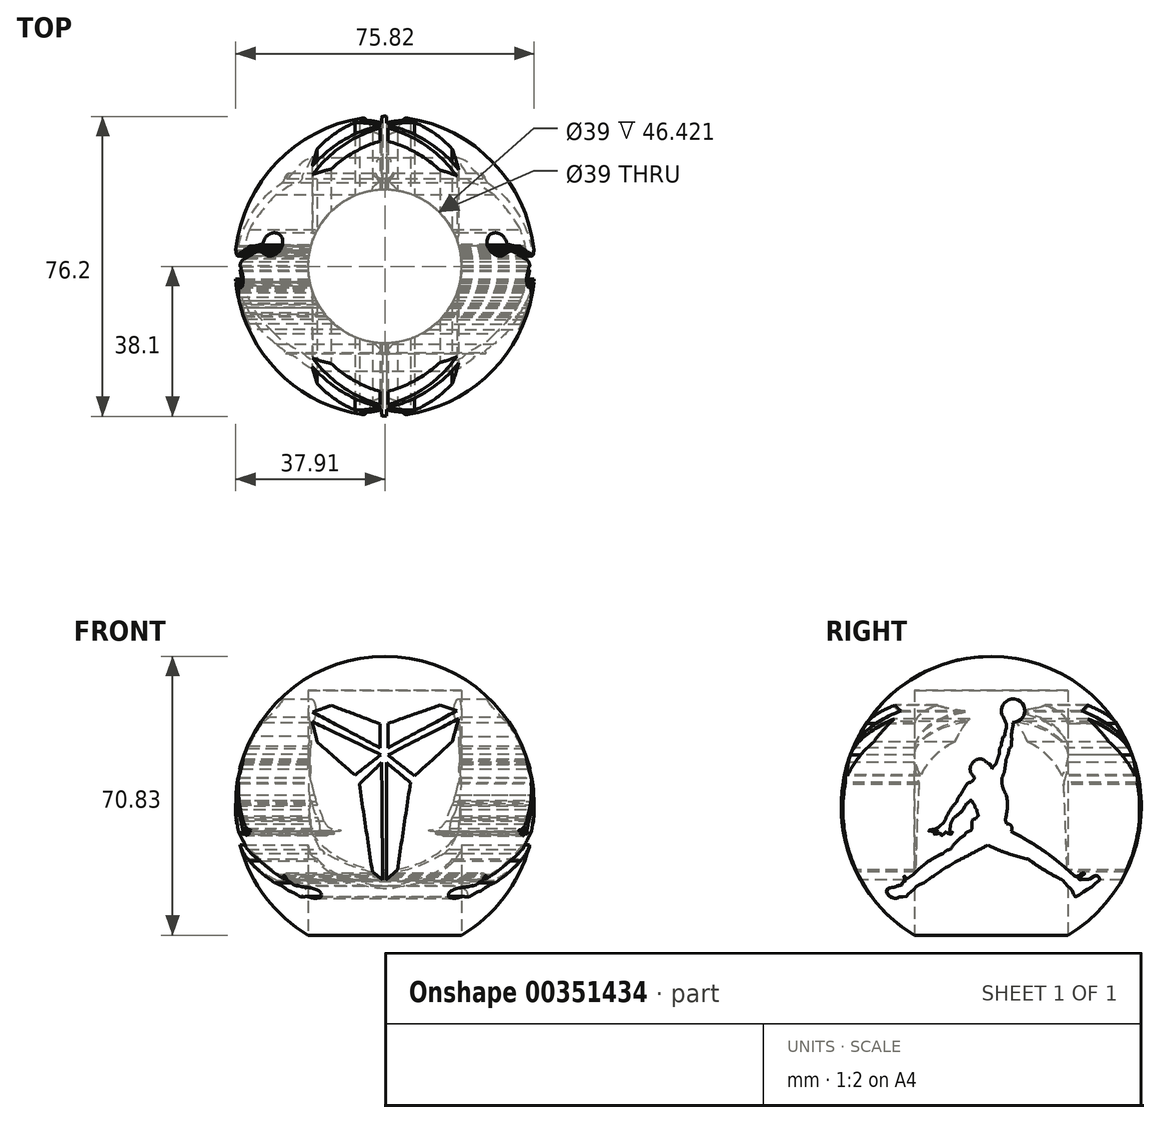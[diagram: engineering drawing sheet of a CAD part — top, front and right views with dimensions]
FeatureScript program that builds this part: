
annotation { "Feature Type Name" : "Feature", "Feature Type Description" : "" }
export const myFeature = defineFeature(function(context is Context, id is Id, definition is map)
    precondition{}
    {
        {
            var Q0;
            Q0=qCreatedBy(makeId("Right.planeOp"),FACE);
            var sketch = newSketch(context, id + "F0", { "sketchPlane" : qUnion([Q0])});
            skLineSegment(sketch, "E0.bottom", {"start": v(38.1, -38.1) * mm, "end": v(-38.1, -38.1) * mm});
            skLineSegment(sketch, "E0.top", {"start": v(38.1, 38.1) * mm, "end": v(-38.1, 38.1) * mm});
            skLineSegment(sketch, "E0.left", {"start": v(38.1, -38.1) * mm, "end": v(38.1, 38.1) * mm});
            skLineSegment(sketch, "E0.right", {"start": v(-38.1, -38.1) * mm, "end": v(-38.1, 38.1) * mm});
            skPoint(sketch, "E0.middle", {"position": v(0, 0) * mm});
            skSolve(sketch);
        }
        {
            var Q0;
            Q0 = qSketchRegion(id + "F0", true);
            extrude(context, id + "F1", {"entities" : qUnion([Q0]), "depth" : 76.2 * mm});
        }
        {
            var Q0;
            Q0=makeQuery(id+"F1.opExtrude","CAP_FACE",FACE,{"disambiguationData":[OSD([sQuery(id+"F0.wireOp",EDGE,"E0.bottom"),sQuery(id+"F0.wireOp",EDGE,"E0.top"),sQuery(id+"F0.wireOp",EDGE,"E0.left"),sQuery(id+"F0.wireOp",EDGE,"E0.right")])],"isStart":false});
            var Q1;
            Q1=makeQuery(id+"F1.opExtrude","CAP_FACE",FACE,{"disambiguationData":[OSD([sQuery(id+"F0.wireOp",EDGE,"E0.bottom"),sQuery(id+"F0.wireOp",EDGE,"E0.top"),sQuery(id+"F0.wireOp",EDGE,"E0.left"),sQuery(id+"F0.wireOp",EDGE,"E0.right")])],"isStart":true});
            var Q2;
            Q2=makeQuery(id+"F1.opExtrude","SWEPT_FACE",FACE,{"disambiguationData":[OSD([sQuery(id+"F0.wireOp",EDGE,"E0.top")])]});
            var Q3;
            Q3=makeQuery(id+"F1.opExtrude","SWEPT_FACE",FACE,{"disambiguationData":[OSD([sQuery(id+"F0.wireOp",EDGE,"E0.bottom")])]});
            fillet(context, id + "F2", {"entities" : qUnion([Q0, Q1, Q2, Q3]), "radius" : 38.1 * mm, "tangentPropagation" : true, "allowEdgeOverflow" : false});
        }
        {
            var Q0;
            Q0=qCreatedBy(makeId("Top.planeOp"),FACE);
            cPlane(context, id + "F3", {"entities" : qUnion([Q0]), "cplaneType" : CPlaneType.OFFSET, "offset" : 38.1 * mm, "width" : 152.4 * mm, "height" : 152.4 * mm});
        }
        {
            var Q0;
            Q0=qCreatedBy(makeId("Front.planeOp"),FACE);
            cPlane(context, id + "F4", {"entities" : qUnion([Q0]), "cplaneType" : CPlaneType.OFFSET, "offset" : 38.1 * mm, "width" : 152.4 * mm, "height" : 152.4 * mm});
        }
        {
            var Q0;
            Q0=qCreatedBy(makeId("Right.planeOp"),FACE);
            cPlane(context, id + "F5", {"entities" : qUnion([Q0]), "cplaneType" : CPlaneType.OFFSET, "offset" : 76.2 * mm, "width" : 152.4 * mm, "height" : 152.4 * mm});
        }
        {
            var Q0;
            Q0=qCreatedBy(id+"F5.planeOp",FACE);
            var sketch = newSketch(context, id + "F6", { "sketchPlane" : qUnion([Q0])});
            skArc(sketch, "E1", {"start": v(21.3, -17.82) * mm, "mid": v(13.59, -11.51) * mm, "end": v(5.03, -6.39) * mm});
            skArc(sketch, "E2", {"start": v(-0.9, -9.83) * mm, "mid": v(4.13, -11.94) * mm, "end": v(9.39, -13.4) * mm});
            skArc(sketch, "E3", {"start": v(9.39, -13.4) * mm, "mid": v(13.68, -16.31) * mm, "end": v(18.22, -18.79) * mm});
            skArc(sketch, "E4", {"start": v(-8.64, -13.89) * mm, "mid": v(-4.75, -11.9) * mm, "end": v(-0.9, -9.83) * mm});
            skArc(sketch, "E5", {"start": v(-8.64, -13.89) * mm, "mid": v(-12.93, -16.51) * mm, "end": v(-17.05, -19.4) * mm});
            skArc(sketch, "E6", {"start": v(-12.18, -11.96) * mm, "mid": v(-16.28, -14.22) * mm, "end": v(-19.8, -17.29) * mm});
            skArc(sketch, "E7", {"start": v(-10.38, -10.97) * mm, "mid": v(-11.4, -11.26) * mm, "end": v(-12.18, -11.96) * mm});
            skArc(sketch, "E8", {"start": v(-6.67, -7.23) * mm, "mid": v(-8.74, -8.89) * mm, "end": v(-10.38, -10.97) * mm});
            skArc(sketch, "E9", {"start": v(-5.69, -6.43) * mm, "mid": v(-6.33, -6.64) * mm, "end": v(-6.67, -7.23) * mm});
            skArc(sketch, "E10", {"start": v(5.03, -6.39) * mm, "mid": v(5.14, -5.01) * mm, "end": v(3.87, -4.48) * mm});
            skFitSpline(sketch, "E11", {"points": [v(-5.69, -6.43) * mm, v(-4.95, -5.8) * mm, v(-4.92, -4.91) * mm, v(-4.95, -4.06) * mm, v(-4.6, -3.34) * mm, v(-3.93, -3.16) * mm], "startDerivative": vector(4.3, 2.53) * mm, "endDerivative": vector(4.01, 0.32) * mm});
            skArc(sketch, "E12", {"start": v(-3.27, -2.4) * mm, "mid": v(-3.63, -2.75) * mm, "end": v(-3.93, -3.16) * mm});
            skArc(sketch, "E13", {"start": v(-3.69, -0.81) * mm, "mid": v(-3.54, -1.62) * mm, "end": v(-3.27, -2.4) * mm});
            skArc(sketch, "E14", {"start": v(-4.13, 0.16) * mm, "mid": v(-4.07, -0.4) * mm, "end": v(-3.69, -0.81) * mm});
            skArc(sketch, "E15", {"start": v(-4.97, 1.44) * mm, "mid": v(-4.6, 0.77) * mm, "end": v(-4.13, 0.16) * mm});
            skArc(sketch, "E16", {"start": v(-4.97, 1.44) * mm, "mid": v(-5.22, 1.45) * mm, "end": v(-5.46, 1.44) * mm});
            skArc(sketch, "E17", {"start": v(-6.32, 0.73) * mm, "mid": v(-5.79, 0.96) * mm, "end": v(-5.46, 1.44) * mm});
            skArc(sketch, "E18", {"start": v(3.87, -4.48) * mm, "mid": v(3.75, -3.94) * mm, "end": v(3.55, -3.43) * mm});
            skArc(sketch, "E19", {"start": v(3.55, -3.43) * mm, "mid": v(4.08, -0.3) * mm, "end": v(3.87, 2.87) * mm});
            skArc(sketch, "E20", {"start": v(2.68, 7.19) * mm, "mid": v(2.9, 4.93) * mm, "end": v(3.87, 2.87) * mm});
            skArc(sketch, "E21", {"start": v(2.68, 7.19) * mm, "mid": v(3.34, 8.86) * mm, "end": v(3.55, 10.64) * mm});
            skArc(sketch, "E22", {"start": v(3.55, 10.64) * mm, "mid": v(3.75, 11.3) * mm, "end": v(3.75, 11.97) * mm});
            skArc(sketch, "E23", {"start": v(3.75, 11.97) * mm, "mid": v(4.3, 13.3) * mm, "end": v(4.49, 14.7) * mm});
            skCircle(sketch, "E24", {"center": v(5.56, 24.31) * mm, "radius": 2.97 * mm});
            skArc(sketch, "E25", {"start": v(-9.37, -2.77) * mm, "mid": v(-7.55, -1.28) * mm, "end": v(-6.32, 0.73) * mm});
            skArc(sketch, "E26", {"start": v(-9.37, -2.77) * mm, "mid": v(-10.16, -4.08) * mm, "end": v(-10.45, -5.59) * mm});
            skPoint(sketch, "E27.3.internal.snap0", {"position": v(-10.16, -4.08) * mm});
            skPoint(sketch, "E27.6.internal.snap0", {"position": v(-10.16, -4.08) * mm});
            skPoint(sketch, "E27.44.internal.snap0", {"position": v(-10.16, -4.08) * mm});
            skFitSpline(sketch, "E27", {"points": [v(-10.45, -5.59) * mm, v(-10.6, -6.09) * mm, v(-10.45, -6.4) * mm, v(-10.16, -6.43) * mm, v(-9.87, -6.53) * mm, v(-9.8, -6.85) * mm, v(-10.16, -7.07) * mm, v(-10.68, -7) * mm, v(-11.06, -6.79) * mm, v(-11.28, -6.53) * mm, v(-11.48, -6.47) * mm, v(-11.71, -6.57) * mm, v(-11.9, -6.79) * mm, v(-12.14, -7.1) * mm, v(-12.44, -7.38) * mm, v(-12.81, -7.48) * mm, v(-12.9, -7.23) * mm, v(-12.72, -6.85) * mm, v(-12.64, -6.7) * mm, v(-12.88, -6.73) * mm, v(-13.26, -6.88) * mm, v(-13.72, -7.03) * mm, v(-14.13, -7.12) * mm, v(-14.43, -7.1) * mm, v(-14.59, -7.02) * mm, v(-14.58, -6.85) * mm, v(-14.32, -6.71) * mm, v(-13.86, -6.5) * mm, v(-13.64, -6.38) * mm, v(-13.58, -6.24) * mm, v(-13.76, -6.22) * mm, v(-14.37, -6.41) * mm, v(-15.17, -6.41) * mm, v(-15.75, -6.32) * mm, v(-15.95, -6.25) * mm, v(-16.02, -6.05) * mm, v(-15.79, -5.99) * mm, v(-15.45, -5.95) * mm, v(-14.82, -5.89) * mm, v(-14.02, -5.69) * mm, v(-13.28, -5.26) * mm, v(-13.1, -5.16) * mm, v(-12.87, -4.91) * mm, v(-12.56, -4.57) * mm, v(-12.15, -4.08) * mm, v(-11.77, -3.69) * mm], "startDerivative": vector(-9.07, -19.11) * mm, "endDerivative": vector(13.84, 13.88) * mm});
            skArc(sketch, "E28", {"start": v(-9.42, 0.39) * mm, "mid": v(-10.78, -1.54) * mm, "end": v(-11.77, -3.69) * mm});
            skArc(sketch, "E29", {"start": v(-8.7, 1.2) * mm, "mid": v(-9.06, 0.8) * mm, "end": v(-9.42, 0.39) * mm});
            skArc(sketch, "E30", {"start": v(-7.8, 2.9) * mm, "mid": v(-8.43, 2.14) * mm, "end": v(-8.7, 1.2) * mm});
            skArc(sketch, "E31", {"start": v(-6.07, 5.8) * mm, "mid": v(-6.98, 4.38) * mm, "end": v(-7.8, 2.9) * mm});
            skArc(sketch, "E32", {"start": v(-5.22, 6.13) * mm, "mid": v(-5.66, 6.01) * mm, "end": v(-6.07, 5.8) * mm});
            skArc(sketch, "E33", {"start": v(-5.22, 6.13) * mm, "mid": v(-4.57, 6.64) * mm, "end": v(-4.21, 7.38) * mm});
            skArc(sketch, "E34", {"start": v(-4.21, 11.51) * mm, "mid": v(-5.36, 9.45) * mm, "end": v(-4.21, 7.38) * mm});
            skArc(sketch, "E35", {"start": v(-1.27, 11.2) * mm, "mid": v(-2.66, 12.05) * mm, "end": v(-4.21, 11.51) * mm});
            skFitSpline(sketch, "E36", {"points": [v(-1.27, 11.2) * mm, v(-1.03, 11.2) * mm, v(-0.82, 10.87) * mm, v(-0.18, 10.7) * mm, v(-0.18, 10.23) * mm, v(0, 10.06) * mm, v(0.14, 9.82) * mm, v(0.19, 9.55) * mm, v(0.2, 9.53) * mm], "startDerivative": vector(2.4, 0.64) * mm, "endDerivative": vector(0.5, -0.27) * mm});
            skArc(sketch, "E37", {"start": v(1.23, 10.78) * mm, "mid": v(0.64, 10.22) * mm, "end": v(0.2, 9.53) * mm});
            skArc(sketch, "E38", {"start": v(2.07, 13.35) * mm, "mid": v(1.62, 12.07) * mm, "end": v(1.23, 10.78) * mm});
            skArc(sketch, "E39", {"start": v(2.55, 15.4) * mm, "mid": v(2.09, 14.43) * mm, "end": v(2.07, 13.35) * mm});
            skFitSpline(sketch, "E40", {"points": [v(2.55, 15.4) * mm, v(2.55, 15.7) * mm, v(2.76, 16.61) * mm, v(3.1, 17.75) * mm, v(3.35, 17.8) * mm, v(3.5, 18.7) * mm, v(3.7, 19.4) * mm, v(3.9, 20.55) * mm, v(3.73, 21.06) * mm, v(3.1, 22.66) * mm, v(3.02, 22.77) * mm], "startDerivative": vector(-0.36, 4.04) * mm, "endDerivative": vector(-1.18, 1.5) * mm});
            skFitSpline(sketch, "E41", {"points": [v(4.49, 14.7) * mm, v(4.96, 15.07) * mm, v(5.14, 16.4) * mm, v(5.18, 17.26) * mm, v(5.1, 17.37) * mm, v(5.25, 18.91) * mm, v(5.43, 20.07) * mm, v(5.58, 20.75) * mm, v(5.36, 21.35) * mm], "startDerivative": vector(5.16, 2.28) * mm, "endDerivative": vector(-2.84, 5.28) * mm});
            skFitSpline(sketch, "E42", {"points": [v(-17.05, -19.4) * mm, v(-19.07, -20.42) * mm, v(-19.97, -21.53) * mm, v(-20.57, -21.75) * mm, v(-21.3, -22.65) * mm, v(-21.72, -23.03) * mm, v(-22.66, -22.95) * mm, v(-23.35, -22.99) * mm, v(-23.86, -23.29) * mm, v(-24.76, -23.33) * mm, v(-25.45, -23.16) * mm, v(-26.6, -21.8) * mm, v(-26.39, -21.1) * mm, v(-25.7, -20.68) * mm, v(-24.42, -20.46) * mm, v(-23.56, -20.08) * mm, v(-23.22, -20.17) * mm, v(-22.62, -19.78) * mm, v(-22.54, -19.4) * mm, v(-22.2, -19.01) * mm, v(-21.85, -19.01) * mm, v(-22.2, -17.98) * mm, v(-21.98, -17.56) * mm, v(-21.5, -18.45) * mm, v(-20.7, -17.98) * mm, v(-19.8, -17.29) * mm, v(-19.8, -17.73) * mm], "startDerivative": vector(-35.97, -12.61) * mm, "endDerivative": vector(-4.01, -21.87) * mm});
            skFitSpline(sketch, "E43", {"points": [v(18.22, -18.79) * mm, v(19.59, -20.4) * mm, v(20.61, -21.43) * mm, v(21.38, -22.97) * mm, v(23.27, -21.77) * mm, v(25.58, -20.4) * mm, v(27.46, -18.79) * mm, v(27.63, -18.79) * mm, v(26.86, -17.58) * mm, v(25.12, -18.44) * mm, v(23.72, -18.55) * mm, v(22.28, -18.55) * mm, v(22.93, -17.55) * mm, v(23.7, -17.2) * mm, v(23.67, -17) * mm, v(22.8, -17.13) * mm, v(22.32, -17.61) * mm, v(22.05, -17.61) * mm, v(21.81, -17.85) * mm, v(21.3, -17.82) * mm], "startDerivative": vector(18.73, -25.11) * mm, "endDerivative": vector(-16.18, 4.5) * mm});
            skSolve(sketch);
        }
        {
            var Q0;
            Q0 = qSketchRegion(id + "F6", true);
            extrude(context, id + "F7", {"entities" : qUnion([Q0]), "operationType" : NewBodyOperationType.REMOVE, "oppositeDirection" : true, "depth" : 77.98 * mm});
        }
        {
            var Q0;
            Q0=qCreatedBy(id+"F4.planeOp",FACE);
            var sketch = newSketch(context, id + "F8", { "sketchPlane" : qUnion([Q0])});
            skLineSegment(sketch, "E44", {"start": v(30.46, 7.92) * mm, "end": v(20.92, 16.34) * mm});
            skLineSegment(sketch, "E45", {"start": v(20.92, 16.34) * mm, "end": v(19.64, 21.53) * mm});
            skLineSegment(sketch, "E46", {"start": v(19.64, 21.53) * mm, "end": v(37.1, 13.1) * mm});
            skLineSegment(sketch, "E47", {"start": v(37.1, 13.1) * mm, "end": v(30.46, 7.92) * mm});
            skLineSegment(sketch, "E48", {"start": v(37.27, 11.11) * mm, "end": v(37.54, -18.7) * mm});
            skLineSegment(sketch, "E49", {"start": v(37.54, -18.7) * mm, "end": v(34.92, -16.6) * mm});
            skLineSegment(sketch, "E50", {"start": v(34.92, -16.6) * mm, "end": v(31.6, 5.6) * mm});
            skLineSegment(sketch, "E51", {"start": v(31.6, 5.6) * mm, "end": v(37.27, 11.11) * mm});
            skLineSegment(sketch, "E52", {"start": v(38.47, 11.11) * mm, "end": v(38.47, -18.7) * mm});
            skLineSegment(sketch, "E53", {"start": v(38.47, -18.7) * mm, "end": v(41.27, -16.12) * mm});
            skLineSegment(sketch, "E54", {"start": v(41.27, -16.12) * mm, "end": v(44.6, 6.02) * mm});
            skLineSegment(sketch, "E55", {"start": v(44.6, 6.02) * mm, "end": v(38.47, 11.11) * mm});
            skLineSegment(sketch, "E56", {"start": v(38.87, 13.04) * mm, "end": v(45.62, 7.73) * mm});
            skLineSegment(sketch, "E57", {"start": v(45.62, 7.73) * mm, "end": v(55.2, 16.39) * mm});
            skLineSegment(sketch, "E58", {"start": v(55.2, 16.39) * mm, "end": v(56.82, 22.26) * mm});
            skLineSegment(sketch, "E59", {"start": v(56.82, 22.26) * mm, "end": v(38.87, 13.04) * mm});
            skLineSegment(sketch, "E60", {"start": v(38.87, 14.85) * mm, "end": v(56.42, 24.28) * mm});
            skLineSegment(sketch, "E61", {"start": v(56.42, 24.28) * mm, "end": v(52.05, 25.7) * mm});
            skLineSegment(sketch, "E62", {"start": v(52.05, 25.7) * mm, "end": v(38.87, 21.04) * mm});
            skLineSegment(sketch, "E63", {"start": v(38.87, 21.04) * mm, "end": v(38.87, 14.85) * mm});
            skLineSegment(sketch, "E64", {"start": v(36.85, 14.85) * mm, "end": v(36.85, 20.97) * mm});
            skLineSegment(sketch, "E65", {"start": v(36.85, 20.97) * mm, "end": v(24.46, 25.62) * mm});
            skLineSegment(sketch, "E66", {"start": v(24.46, 25.62) * mm, "end": v(19.74, 23.95) * mm});
            skLineSegment(sketch, "E67", {"start": v(19.74, 23.95) * mm, "end": v(36.85, 14.85) * mm});
            skSolve(sketch);
        }
        {
            var Q0;
            Q0 = qSketchRegion(id + "F8", true);
            extrude(context, id + "F9", {"entities" : qUnion([Q0]), "operationType" : NewBodyOperationType.REMOVE, "oppositeDirection" : true, "depth" : 100.84 * mm});
        }
        {
            var Q0;
            Q0=qCreatedBy(makeId("Top.planeOp"),FACE);
            cPlane(context, id + "F10", {"entities" : qUnion([Q0]), "cplaneType" : CPlaneType.OFFSET, "offset" : 38.86 * mm, "oppositeDirection" : true, "width" : 152.4 * mm, "height" : 152.4 * mm});
        }
        {
            var Q0;
            Q0=qCreatedBy(id+"F10.planeOp",FACE);
            var sketch = newSketch(context, id + "F11", { "sketchPlane" : qUnion([Q0])});
            skLineSegment(sketch, "E68.bottom", {"start": v(76.2, 38.1) * mm, "end": v(0, 38.1) * mm, "construction": true});
            skLineSegment(sketch, "E68.top", {"start": v(76.2, -38.1) * mm, "end": v(0, -38.1) * mm, "construction": true});
            skLineSegment(sketch, "E68.left", {"start": v(76.2, 38.1) * mm, "end": v(76.2, -38.1) * mm, "construction": true});
            skLineSegment(sketch, "E68.right", {"start": v(0, 38.1) * mm, "end": v(0, -38.1) * mm, "construction": true});
            skLineSegment(sketch, "E69", {"start": v(0, -38.1) * mm, "end": v(76.2, 38.1) * mm, "construction": true});
            skLineSegment(sketch, "E70", {"start": v(76.2, -38.1) * mm, "end": v(0, 38.1) * mm, "construction": true});
            skPoint(sketch, "E71", {"position": v(38.1, 0) * mm});
            skCircle(sketch, "E72", {"center": v(38.1, 0) * mm, "radius": 19.5 * mm});
            skSolve(sketch);
        }
        {
            var Q0;
            Q0 = qSketchRegion(id + "F11", true);
            extrude(context, id + "F12", {"entities" : qUnion([Q0]), "operationType" : NewBodyOperationType.REMOVE, "depth" : 68.33 * mm});
        }
    });
